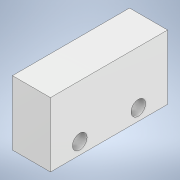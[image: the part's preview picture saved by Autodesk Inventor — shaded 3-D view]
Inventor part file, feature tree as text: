
AUTODESK INVENTOR PART (.ipt)
format: ipt  version: 2020 (Build 240168000, 168)  size: 105,472 bytes
history: native  units: mm
features: extrude x2, sketch x2, other x1
ambient origin geometry x8: Origin, YZ Plane, XZ Plane, XY Plane, X Axis, Y Axis, Z Axis, Center Point
bodies: Body1 (feature_tree)
feature tree (5):
  other  "Bryła1"
  extrude  "Wyciągnięcie proste1"  Depth=20.0mm
  extrude  "Wyciągnięcie proste2"  Depth=11.0mm
  sketch  "Szkic1"
  sketch  "Szkic2"
